# Revit family: Plum Fix_Toilet_Argent_Grace Compact Wall Faced Hygienic Flush_ S&P Trap
name_source: partatom
category: Plumbing Fixtures
revit_build: Autodesk Revit 2016 (Build: 20190508_0715(x64)
units: mm (PartAtom-declared; Revit-internal decimal feet)

## family parameters
Always vertical = Yes
Cut with Voids When Loaded = No
OmniClass Number = 23.45.05.21.11
OmniClass Title = Water Closets
Part Type = Normal
Room Calculation Point = No
Round Connector Dimension = Use Diameter
Shared = No
Work Plane-Based = No

## types (1)
- S/P-Trap (8H157R001S4B)
    Body Material = z_Argent_Ceramic White
    CW Connection = Yes
    Cost = 0 $
    Description = Grace Compact HygienicFlush Wall Faced WELS 4 Star / 4.5/3L (3.5Avg)Flush
    HW Connection = No
    IfcExportAs = IfcSanitaryTerminal
    IfcExportType = TOILETPAN
    Manufacturer = Argent
    Manufacturer_Overall Depth = 535 mm
    Manufacturer_Overall Height = 426 mm
    Manufacturer_Overall Width = 370 mm
    Manufacturer_Spec Code = 8H157R001S4B
    Manufacturer_URL__Product Specific = https://www.argentaust.com.au
    Model = 8H157R001S4B
    ModifiedIssue_ANZRS = 20200415 $
    Toilet P Trap = Yes
    Toilet S Trap = No
    Type Comments = S/P-Trap
    URL = https://www.argentaust.com.au
    Uniclass2015Code = Pr_40_20_93_97
    Uniclass2015Title = WC suites
    Uniclass2015Version = Products v1.17
    Vent Connection = No
    Waste Connection = Yes

## geometry (parser evidence)
native form markers: Sweep x2
no freeform markers — native parametric forms only
